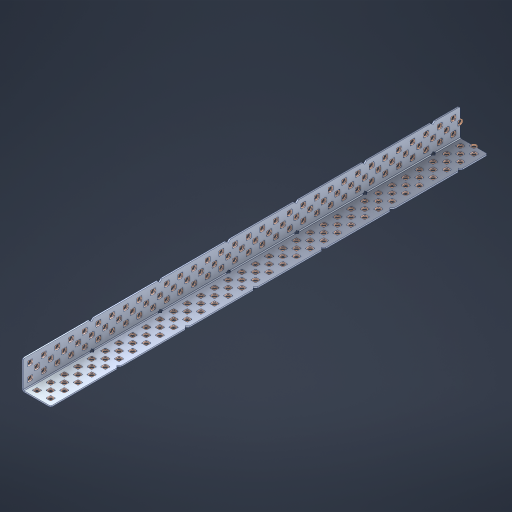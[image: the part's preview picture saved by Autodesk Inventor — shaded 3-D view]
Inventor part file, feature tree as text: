
AUTODESK INVENTOR PART (.ipt)
format: ipt  version: 2023 (Build 270158000, 158)  size: 2,181,120 bytes
history: native  units: in
note: dims shown in document units (in); Inventor stores cm internally (conversion verified against a paired STEP export)
features: other x198, extrude x190, sheet_metal_op x8, sketch x7, pattern_linear x2, mirror x1, chamfer x1
ambient origin geometry x8: Origin, YZ Plane, XZ Plane, XY Plane, X Axis, Y Axis, Z Axis, Center Point
bodies: Solid1 (feature_tree), Body (feature_tree)
feature tree (407):
  sheet_metal_op  "Flanges"
  sheet_metal_op  "Body Pattern"
  pattern_linear  "Center Pattern"  Spacing1=1.0in  [1 undecoded]
  other  "Arc Length"
  pattern_linear  "Notch Pattern"  Spacing1=0.1875in  [1 undecoded]
  other  "Diagonal Plane"
  mirror  "Everything Mirrored"
  chamfer  "End Chamfer"
  sketch  "Sketch1"  dims[d0=1.0in]
  other  "Plate1"
  sketch  "Sketch2"  dims[d1=16.0in]
  other  "Plate2"
  sheet_metal_op  "Bend1"
  sheet_metal_op  "Corner1"
  sketch  "Sketch8"  dims[d2=0.0469in]
  sketch  "Sketch9"  dims[d3=0.0469in]
  other  "Srf91"
  sheet_metal_op  "Body Pattern Sketch"
  other  "Srf92"
  sketch  "Sketch13"  dims[d4=0.0234in]
  sketch  "Sketch15"  dims[d5=0.0938in]
  sketch  "Sketch16"  dims[d6=0.0469in d7=1.0in d8=90.0deg d9=0.0312in d10=0.1875in d11=0.0469in d12=0.0469in d49=0.182in d50=0.02in d52=0.25in d53=0.0469in d54=0.0in d55=0.172in d56=1.0in d57=0.0in d60=12.5984in d62=0.5in d63=0.7874in d65=0.5in d85=0.1473in d86=0.1659in d89=0.0469in d90=0.0in d91=0.04in d92=0.0491in d95=2.5in d96=0.04in d97=0.25in d98=45.0deg d99=0.25in d106=0.182in d107=0.02in d108=0.5in d110=0.0469in d111=0.0in d112=0.172in d113=0.5in d114=0.0in d117=0.5in d123=0.25in d125=0.25in d126=0.0491in d127=0.1227in d128=0.08in d129=0.04in d130=2.5in]
  other  "Srf786"
  other  "Srf856"
  other  "Srf857"
  other  "Srf858"
  other  "Srf859"
  other  "Srf860"
  other  "Srf861"
  other  "Srf889"
  other  "Srf890"
  other  "Srf891"
  other  "Srf1275"
  other  "Srf1276"
  other  "Srf1278"
  other  "Srf1279"
  other  "Srf1280"
  other  "Srf1281"
  other  "Srf1282"
  other  "Srf1283"
  other  "Srf1277"
  other  "Srf1285"
  other  "Srf1286"
  other  "Srf1287"
  other  "Srf1383"
  other  "Srf1384"
  other  "Srf1385"
  other  "Srf1386"
  other  "Srf1387"
  other  "Srf1388"
  other  "Srf1389"
  other  "Srf1390"
  other  "Srf1391"
  other  "Srf1392"
  other  "Srf1393"
  other  "Srf1394"
  other  "Srf1395"
  other  "Srf1396"
  other  "Srf1397"
  other  "Srf1398"
  other  "Srf1399"
  other  "Srf1400"
  other  "Srf1401"
  other  "Srf1402"
  other  "Srf1403"
  other  "Srf1404"
  other  "Srf1405"
  other  "Srf1406"
  other  "Srf1407"
  other  "Srf1408"
  other  "Srf1409"
  other  "Srf1410"
  other  "Srf1411"
  other  "Srf1412"
  other  "Srf1413"
  other  "Srf1414"
  other  "Srf1415"
  other  "Srf1416"
  other  "Srf1417"
  other  "Srf1418"
  other  "Srf1419"
  other  "Srf1420"
  other  "Srf1421"
  other  "Srf1422"
  other  "Srf1423"
  other  "Srf1424"
  other  "Srf1425"
  other  "Srf1426"
  other  "Srf1427"
  other  "Srf1428"
  other  "Srf1429"
  other  "Srf1430"
  other  "Srf1431"
  other  "Srf1432"
  other  "Srf1433"
  other  "Srf1434"
  other  "Srf1435"
  other  "Srf1436"
  other  "Srf1437"
  other  "Srf1438"
  other  "Srf1445"
  other  "Srf1446"
  other  "Srf1447"
  other  "Srf1448"
  other  "Srf1449"
  other  "Srf1450"
  other  "Srf1451"
  other  "Srf1452"
  other  "Srf1453"
  other  "Srf1454"
  other  "Srf1455"
  other  "Srf1456"
  other  "Srf1457"
  other  "Srf1458"
  other  "Srf1459"
  other  "Srf1460"
  other  "Srf1461"
  other  "Srf1462"
  other  "Srf1463"
  other  "Srf1464"
  other  "Srf1465"
  other  "Srf1466"
  other  "Srf1467"
  other  "Srf1468"
  other  "Srf1469"
  other  "Srf1470"
  other  "Srf1471"
  other  "Srf1472"
  other  "Srf1475"
  other  "Srf1476"
  other  "Srf1477"
  other  "Srf1478"
  other  "Srf1479"
  other  "Srf1480"
  other  "Srf1481"
  other  "Srf1482"
  other  "Srf1483"
  other  "Srf1484"
  other  "Srf1485"
  other  "Srf1486"
  other  "Srf1487"
  other  "Srf1488"
  other  "Srf1489"
  other  "Srf1490"
  other  "Srf1491"
  other  "Srf1492"
  other  "Srf1493"
  other  "Srf1494"
  other  "Srf1495"
  other  "Srf1496"
  other  "Srf1497"
  other  "Srf1498"
  other  "Srf1499"
  other  "Srf1500"
  other  "Srf1501"
  other  "Srf1502"
  other  "Srf1503"
  other  "Srf1504"
  other  "Srf1505"
  other  "Srf1506"
  other  "Srf1507"
  other  "Srf1508"
  other  "Srf1509"
  other  "Srf1510"
  other  "Srf1511"
  other  "Srf1512"
  other  "Srf1513"
  other  "Srf1514"
  other  "Srf1515"
  other  "Srf1516"
  other  "Srf1517"
  other  "Srf1518"
  other  "Srf1519"
  other  "Srf1520"
  other  "Srf1521"
  other  "Srf1522"
  other  "Srf1523"
  other  "Srf1524"
  other  "Srf1525"
  other  "Srf1526"
  other  "Srf1527"
  other  "Srf1528"
  other  "Srf1529"
  other  "Srf1530"
  other  "Srf1537"
  other  "Srf1538"
  other  "Srf1539"
  other  "Srf1540"
  other  "Srf1541"
  other  "Srf1542"
  other  "Srf1543"
  other  "Srf1544"
  other  "Srf1545"
  other  "Srf1546"
  other  "Srf1547"
  other  "Srf1548"
  other  "Srf1549"
  other  "Srf1550"
  other  "Srf1551"
  other  "Srf1552"
  other  "Srf1553"
  other  "Srf1554"
  other  "Srf1555"
  other  "Srf1556"
  other  "Srf1557"
  other  "Srf1558"
  other  "Srf1559"
  other  "Srf1560"
  other  "Srf1561"
  other  "Srf1562"
  other  "Srf1563"
  other  "Srf1564"
  sheet_metal_op  "Body Stamp"
  sheet_metal_op  "Body Circle"
  other  "Center Stamp"
  other  "Center Circle"
  sheet_metal_op  "Notch"
  extrude  "ExtrusionSrf92"  Depth=0.0469in
  extrude  "ExtrusionSrf856"  Depth=0.0469in
  extrude  "ExtrusionSrf857"  Depth=0.182in
  extrude  "ExtrusionSrf858"  Depth=0.02in
  extrude  "ExtrusionSrf859"  Depth=0.25in
  extrude  "ExtrusionSrf860"  Depth=0.0469in
  extrude  "ExtrusionSrf861"  TaperAngle=0.0deg  [1 undecoded]
  extrude  "ExtrusionSrf889"  Depth=2.5in
  extrude  "ExtrusionSrf890"  Depth=1.0in TaperAngle=0.0deg
  extrude  "ExtrusionSrf891"  Depth=2.5in
  extrude  "ExtrusionSrf1275"  Depth=0.5in
  extrude  "ExtrusionSrf1276"  Depth=2.5in
  extrude  "ExtrusionSrf1277"  Depth=2.5in
  extrude  "ExtrusionSrf1278"  Depth=0.0469in
  extrude  "ExtrusionSrf1279"  Depth=2.5in TaperAngle=0.0deg
  extrude  "ExtrusionSrf1280"  Depth=2.5in
  extrude  "ExtrusionSrf1281"  Depth=0.25in TaperAngle=45.0deg
  extrude  "ExtrusionSrf1282"  Depth=0.25in
  extrude  "ExtrusionSrf1345"  Depth=0.182in
  extrude  "ExtrusionSrf1346"  Depth=0.02in
  extrude  "ExtrusionSrf1347"  Depth=0.5in
  extrude  "ExtrusionSrf1348"  Depth=0.0469in
  extrude  "ExtrusionSrf1383"  TaperAngle=0.0deg  [1 undecoded]
  extrude  "ExtrusionSrf1384"  Depth=2.5in
  extrude  "ExtrusionSrf1385"  Depth=0.5in TaperAngle=0.0deg
  extrude  "ExtrusionSrf1386"  Depth=0.5in
  extrude  "ExtrusionSrf1387"  Depth=0.25in
  extrude  "ExtrusionSrf1388"  Depth=0.25in
  extrude  "ExtrusionSrf1389"  Depth=2.5in
  extrude  "ExtrusionSrf1390"  Depth=2.5in
  extrude  "ExtrusionSrf1391"  Depth=2.5in
  extrude  "ExtrusionSrf1392"  Depth=2.5in
  extrude  "ExtrusionSrf1393"  Depth=2.5in
  extrude  "ExtrusionSrf1394"  [1 undecoded]
  extrude  "ExtrusionSrf1395"  [1 undecoded]
  extrude  "ExtrusionSrf1396"  [1 undecoded]
  extrude  "ExtrusionSrf1397"  [1 undecoded]
  extrude  "ExtrusionSrf1398"  [1 undecoded]
  extrude  "ExtrusionSrf1399"  [1 undecoded]
  extrude  "ExtrusionSrf1400"  [1 undecoded]
  extrude  "ExtrusionSrf1401"  [1 undecoded]
  extrude  "ExtrusionSrf1402"  [1 undecoded]
  extrude  "ExtrusionSrf1403"  [1 undecoded]
  extrude  "ExtrusionSrf1404"  [1 undecoded]
  extrude  "ExtrusionSrf1405"  [1 undecoded]
  extrude  "ExtrusionSrf1406"  [1 undecoded]
  extrude  "ExtrusionSrf1407"  [1 undecoded]
  extrude  "ExtrusionSrf1408"  [1 undecoded]
  extrude  "ExtrusionSrf1409"  [1 undecoded]
  extrude  "ExtrusionSrf1410"  [1 undecoded]
  extrude  "ExtrusionSrf1411"  [1 undecoded]
  extrude  "ExtrusionSrf1412"  [1 undecoded]
  extrude  "ExtrusionSrf1413"  [1 undecoded]
  extrude  "ExtrusionSrf1414"  [1 undecoded]
  extrude  "ExtrusionSrf1415"  [1 undecoded]
  extrude  "ExtrusionSrf1416"  [1 undecoded]
  extrude  "ExtrusionSrf1417"  [1 undecoded]
  extrude  "ExtrusionSrf1418"  [1 undecoded]
  extrude  "ExtrusionSrf1419"  [1 undecoded]
  extrude  "ExtrusionSrf1420"  [1 undecoded]
  extrude  "ExtrusionSrf1421"  [1 undecoded]
  extrude  "ExtrusionSrf1422"  [1 undecoded]
  extrude  "ExtrusionSrf1423"  [1 undecoded]
  extrude  "ExtrusionSrf1424"  [1 undecoded]
  extrude  "ExtrusionSrf1425"  [1 undecoded]
  extrude  "ExtrusionSrf1426"  [1 undecoded]
  extrude  "ExtrusionSrf1427"  [1 undecoded]
  extrude  "ExtrusionSrf1428"  [1 undecoded]
  extrude  "ExtrusionSrf1429"  [1 undecoded]
  extrude  "ExtrusionSrf1430"  [1 undecoded]
  extrude  "ExtrusionSrf1431"  [1 undecoded]
  extrude  "ExtrusionSrf1432"  [1 undecoded]
  extrude  "ExtrusionSrf1433"  [1 undecoded]
  extrude  "ExtrusionSrf1434"  [1 undecoded]
  extrude  "ExtrusionSrf1435"  [1 undecoded]
  extrude  "ExtrusionSrf1436"  [1 undecoded]
  extrude  "ExtrusionSrf1437"  [1 undecoded]
  extrude  "ExtrusionSrf1438"  [1 undecoded]
  extrude  "ExtrusionSrf1445"  [1 undecoded]
  extrude  "ExtrusionSrf1446"  [1 undecoded]
  extrude  "ExtrusionSrf1447"  [1 undecoded]
  extrude  "ExtrusionSrf1448"  [1 undecoded]
  extrude  "ExtrusionSrf1449"  [1 undecoded]
  extrude  "ExtrusionSrf1450"  [1 undecoded]
  extrude  "ExtrusionSrf1451"  [1 undecoded]
  extrude  "ExtrusionSrf1452"  [1 undecoded]
  extrude  "ExtrusionSrf1453"  [1 undecoded]
  extrude  "ExtrusionSrf1454"  [1 undecoded]
  extrude  "ExtrusionSrf1455"  [1 undecoded]
  extrude  "ExtrusionSrf1456"  [1 undecoded]
  extrude  "ExtrusionSrf1457"  [1 undecoded]
  extrude  "ExtrusionSrf1458"  [1 undecoded]
  extrude  "ExtrusionSrf1459"  [1 undecoded]
  extrude  "ExtrusionSrf1460"  [1 undecoded]
  extrude  "ExtrusionSrf1461"  [1 undecoded]
  extrude  "ExtrusionSrf1462"  [1 undecoded]
  extrude  "ExtrusionSrf1463"  [1 undecoded]
  extrude  "ExtrusionSrf1464"  [1 undecoded]
  extrude  "ExtrusionSrf1465"  [1 undecoded]
  extrude  "ExtrusionSrf1466"  [1 undecoded]
  extrude  "ExtrusionSrf1467"  [1 undecoded]
  extrude  "ExtrusionSrf1468"  [1 undecoded]
  extrude  "ExtrusionSrf1469"  [1 undecoded]
  extrude  "ExtrusionSrf1470"  [1 undecoded]
  extrude  "ExtrusionSrf1471"  [1 undecoded]
  extrude  "ExtrusionSrf1472"  [1 undecoded]
  extrude  "ExtrusionSrf1475"  [1 undecoded]
  extrude  "ExtrusionSrf1476"  [1 undecoded]
  extrude  "ExtrusionSrf1477"  [1 undecoded]
  extrude  "ExtrusionSrf1478"  [1 undecoded]
  extrude  "ExtrusionSrf1479"  [1 undecoded]
  extrude  "ExtrusionSrf1480"  [1 undecoded]
  extrude  "ExtrusionSrf1481"  [1 undecoded]
  extrude  "ExtrusionSrf1482"  [1 undecoded]
  extrude  "ExtrusionSrf1483"  [1 undecoded]
  extrude  "ExtrusionSrf1484"  [1 undecoded]
  extrude  "ExtrusionSrf1485"  [1 undecoded]
  extrude  "ExtrusionSrf1486"  [1 undecoded]
  extrude  "ExtrusionSrf1487"  [1 undecoded]
  extrude  "ExtrusionSrf1488"  [1 undecoded]
  extrude  "ExtrusionSrf1489"  [1 undecoded]
  extrude  "ExtrusionSrf1490"  [1 undecoded]
  extrude  "ExtrusionSrf1491"  [1 undecoded]
  extrude  "ExtrusionSrf1492"  [1 undecoded]
  extrude  "ExtrusionSrf1493"  [1 undecoded]
  extrude  "ExtrusionSrf1494"  [1 undecoded]
  extrude  "ExtrusionSrf1495"  [1 undecoded]
  extrude  "ExtrusionSrf1496"  [1 undecoded]
  extrude  "ExtrusionSrf1497"  [1 undecoded]
  extrude  "ExtrusionSrf1498"  [1 undecoded]
  extrude  "ExtrusionSrf1499"  [1 undecoded]
  extrude  "ExtrusionSrf1500"  [1 undecoded]
  extrude  "ExtrusionSrf1501"  [1 undecoded]
  extrude  "ExtrusionSrf1502"  [1 undecoded]
  extrude  "ExtrusionSrf1503"  [1 undecoded]
  extrude  "ExtrusionSrf1504"  [1 undecoded]
  extrude  "ExtrusionSrf1505"  [1 undecoded]
  extrude  "ExtrusionSrf1506"  [1 undecoded]
  extrude  "ExtrusionSrf1507"  [1 undecoded]
  extrude  "ExtrusionSrf1508"  [1 undecoded]
  extrude  "ExtrusionSrf1509"  [1 undecoded]
  extrude  "ExtrusionSrf1510"  [1 undecoded]
  extrude  "ExtrusionSrf1511"  [1 undecoded]
  extrude  "ExtrusionSrf1512"  [1 undecoded]
  extrude  "ExtrusionSrf1513"  [1 undecoded]
  extrude  "ExtrusionSrf1514"  [1 undecoded]
  extrude  "ExtrusionSrf1515"  [1 undecoded]
  extrude  "ExtrusionSrf1516"  [1 undecoded]
  extrude  "ExtrusionSrf1517"  [1 undecoded]
  extrude  "ExtrusionSrf1518"  [1 undecoded]
  extrude  "ExtrusionSrf1519"  [1 undecoded]
  extrude  "ExtrusionSrf1520"  [1 undecoded]
  extrude  "ExtrusionSrf1521"  [1 undecoded]
  extrude  "ExtrusionSrf1522"  [1 undecoded]
  extrude  "ExtrusionSrf1523"  [1 undecoded]
  extrude  "ExtrusionSrf1524"  [1 undecoded]
  extrude  "ExtrusionSrf1525"  [1 undecoded]
  extrude  "ExtrusionSrf1526"  [1 undecoded]
  extrude  "ExtrusionSrf1527"  [1 undecoded]
  extrude  "ExtrusionSrf1528"  [1 undecoded]
  extrude  "ExtrusionSrf1529"  [1 undecoded]
  extrude  "ExtrusionSrf1530"  [1 undecoded]
  extrude  "ExtrusionSrf1537"  [1 undecoded]
  extrude  "ExtrusionSrf1538"  [1 undecoded]
  extrude  "ExtrusionSrf1539"  [1 undecoded]
  extrude  "ExtrusionSrf1540"  [1 undecoded]
  extrude  "ExtrusionSrf1541"  [1 undecoded]
  extrude  "ExtrusionSrf1542"  [1 undecoded]
  extrude  "ExtrusionSrf1543"  [1 undecoded]
  extrude  "ExtrusionSrf1544"  [1 undecoded]
  extrude  "ExtrusionSrf1545"  [1 undecoded]
  extrude  "ExtrusionSrf1546"  [1 undecoded]
  extrude  "ExtrusionSrf1547"  [1 undecoded]
  extrude  "ExtrusionSrf1548"  [1 undecoded]
  extrude  "ExtrusionSrf1549"  [1 undecoded]
  extrude  "ExtrusionSrf1550"  [1 undecoded]
  extrude  "ExtrusionSrf1551"  [1 undecoded]
  extrude  "ExtrusionSrf1552"  [1 undecoded]
  extrude  "ExtrusionSrf1553"  [1 undecoded]
  extrude  "ExtrusionSrf1554"  [1 undecoded]
  extrude  "ExtrusionSrf1555"  [1 undecoded]
  extrude  "ExtrusionSrf1556"  [1 undecoded]
  extrude  "ExtrusionSrf1557"  [1 undecoded]
  extrude  "ExtrusionSrf1558"  [1 undecoded]
  extrude  "ExtrusionSrf1559"  [1 undecoded]
  extrude  "ExtrusionSrf1560"  [1 undecoded]
  extrude  "ExtrusionSrf1561"  [1 undecoded]
  extrude  "ExtrusionSrf1562"  [1 undecoded]
  extrude  "ExtrusionSrf1563"  [1 undecoded]
  extrude  "ExtrusionSrf1564"  [1 undecoded]
note: 161 required parameter values undecoded (feature->parameter linkage not recoverable at this tier; creation-order binding heuristic only, values carry confidence <= 0.55)
